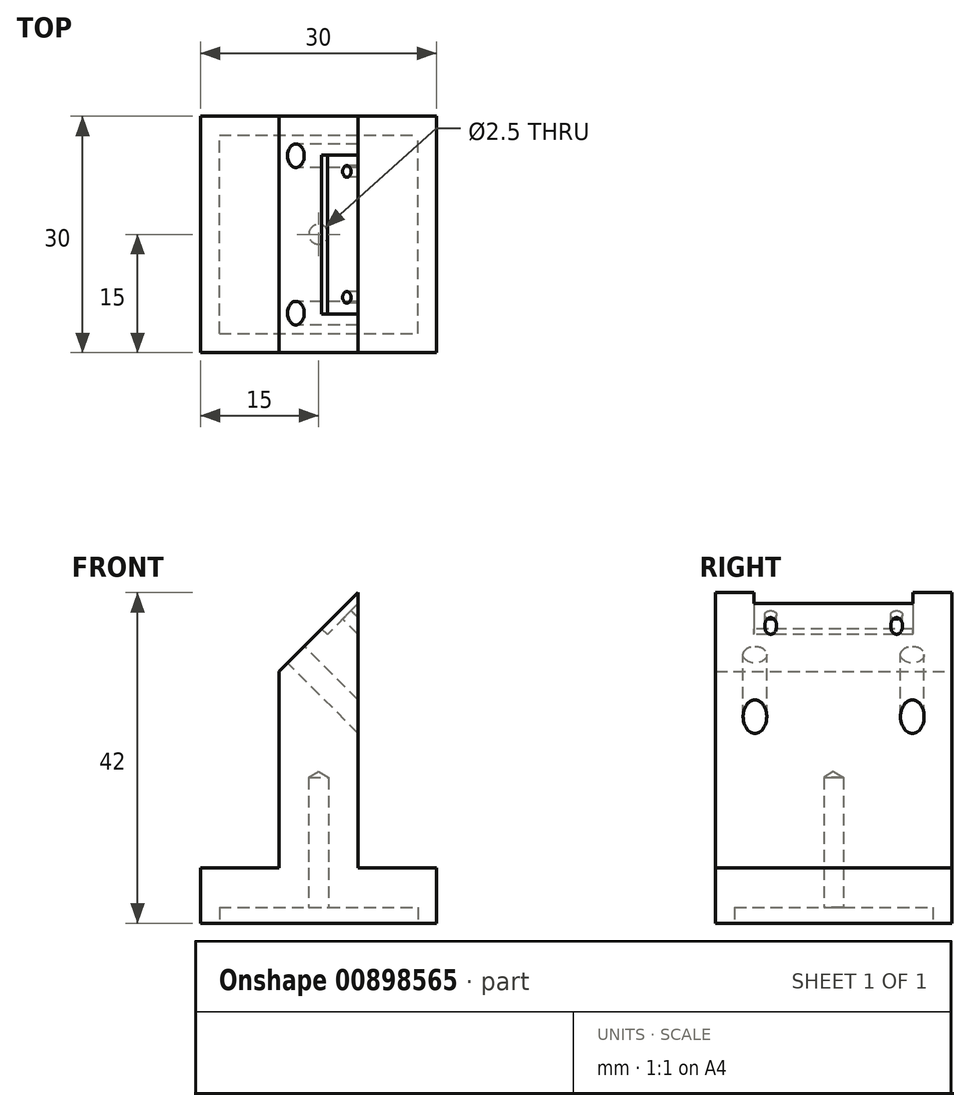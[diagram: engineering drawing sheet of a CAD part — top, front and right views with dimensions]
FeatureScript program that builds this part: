
annotation { "Feature Type Name" : "Feature", "Feature Type Description" : "" }
export const myFeature = defineFeature(function(context is Context, id is Id, definition is map)
    precondition{}
    {
        {
            var Q0;
            Q0=qCreatedBy(makeId("Top.planeOp"),FACE);
            var sketch = newSketch(context, id + "F0", { "sketchPlane" : qUnion([Q0])});
            skLineSegment(sketch, "E0.bottom", {"start": v(-15, 15) * mm, "end": v(15, 15) * mm});
            skLineSegment(sketch, "E0.top", {"start": v(-15, -15) * mm, "end": v(15, -15) * mm});
            skLineSegment(sketch, "E0.left", {"start": v(-15, 15) * mm, "end": v(-15, -15) * mm});
            skLineSegment(sketch, "E0.right", {"start": v(15, 15) * mm, "end": v(15, -15) * mm});
            skLineSegment(sketch, "E1", {"start": v(-15, 15) * mm, "end": v(15, -15) * mm, "construction": true});
            skLineSegment(sketch, "E2", {"start": v(-15, -15) * mm, "end": v(15, 15) * mm, "construction": true});
            skPoint(sketch, "E3", {"position": v(0, 0) * mm});
            skSolve(sketch);
        }
        {
            var Q0;
            Q0 = qSketchRegion(id + "F0", true);
            extrude(context, id + "F1", {"entities" : qUnion([Q0]), "depth" : 7 * mm, "offsetDistance" : 25 * mm});
        }
        {
            var Q0;
            Q0=makeQuery(id+"F1.opExtrude","CAP_FACE",FACE,{"disambiguationData":[OSD([sQuery(id+"F0.wireOp",EDGE,"E0.bottom"),sQuery(id+"F0.wireOp",EDGE,"E0.top"),sQuery(id+"F0.wireOp",EDGE,"E0.left"),sQuery(id+"F0.wireOp",EDGE,"E0.right")])],"isStart":false});
            var sketch = newSketch(context, id + "F2", { "sketchPlane" : qUnion([Q0])});
            skLineSegment(sketch, "E4.bottom", {"start": v(-5, 15) * mm, "end": v(5, 15) * mm});
            skLineSegment(sketch, "E4.top", {"start": v(-5, -15) * mm, "end": v(5, -15) * mm});
            skLineSegment(sketch, "E4.left", {"start": v(-5, 15) * mm, "end": v(-5, -15) * mm});
            skLineSegment(sketch, "E4.right", {"start": v(5, 15) * mm, "end": v(5, -15) * mm});
            skLineSegment(sketch, "E5", {"start": v(5, 15) * mm, "end": v(-5, -15) * mm, "construction": true});
            skLineSegment(sketch, "E6", {"start": v(-15, -15) * mm, "end": v(-15, 15) * mm});
            skLineSegment(sketch, "E7", {"start": v(-5, 15) * mm, "end": v(5, -15) * mm, "construction": true});
            skPoint(sketch, "E8", {"position": v(0, 0) * mm});
            skSolve(sketch);
        }
        {
            var Q0;
            Q0=makeQuery(id+"F2.imprint","IMPRINT",FACE,{"disambiguationData":[TD([[makeQuery(id+"F2.imprint","IMPRINT",EDGE,{"derivedFrom":sQuery(id+"F2.wireOp",EDGE,"E4.bottom")}),-1.0]])]});
            extrude(context, id + "F3", {"entities" : qUnion([Q0]), "operationType" : NewBodyOperationType.ADD, "depth" : 35 * mm, "offsetDistance" : 25 * mm});
        }
        {
            var Q0;
            Q0=makeQuery(id+"F3.opExtrude","CAP_EDGE",EDGE,{"disambiguationData":[OSD([sQuery(id+"F2.wireOp",EDGE,"E4.left")])],"isStart":false});
            chamfer(context, id + "F4", {"entities" : qUnion([Q0]), "width" : 10 * mm, "tangentPropagation" : true});
        }
        {
            var Q0;
            Q0=makeQuery(id+"F1.opExtrude","CAP_FACE",FACE,{"disambiguationData":[OSD([sQuery(id+"F0.wireOp",EDGE,"E0.bottom"),sQuery(id+"F0.wireOp",EDGE,"E0.top"),sQuery(id+"F0.wireOp",EDGE,"E0.left"),sQuery(id+"F0.wireOp",EDGE,"E0.right")])],"isStart":true});
            var sketch = newSketch(context, id + "F5", { "sketchPlane" : qUnion([Q0])});
            skLineSegment(sketch, "E9.bottom", {"start": v(-12.6, 12.6) * mm, "end": v(12.6, 12.6) * mm});
            skLineSegment(sketch, "E9.top", {"start": v(-12.6, -12.6) * mm, "end": v(12.6, -12.6) * mm});
            skLineSegment(sketch, "E9.left", {"start": v(-12.6, 12.6) * mm, "end": v(-12.6, -12.6) * mm});
            skLineSegment(sketch, "E9.right", {"start": v(12.6, 12.6) * mm, "end": v(12.6, -12.6) * mm});
            skPoint(sketch, "E9.middle", {"position": v(0, 0) * mm});
            skSolve(sketch);
        }
        {
            var Q0;
            Q0=makeQuery(id+"F5.imprint","IMPRINT",FACE,{"disambiguationData":[TD([[makeQuery(id+"F5.imprint","IMPRINT",EDGE,{"derivedFrom":sQuery(id+"F5.wireOp",EDGE,"E9.bottom")}),-1.0]])]});
            extrude(context, id + "F6", {"entities" : qUnion([Q0]), "oppositeDirection" : true, "depth" : 2 * mm, "offsetDistance" : 25 * mm});
        }
        {
            var Q0;
            Q0=makeQuery(id+"F6.opExtrude","SWEPT_BODY",BODY,{"disambiguationData":[OSD([sQuery(id+"F5.wireOp",EDGE,"E9.bottom"),sQuery(id+"F5.wireOp",EDGE,"E9.top"),sQuery(id+"F5.wireOp",EDGE,"E9.left"),sQuery(id+"F5.wireOp",EDGE,"E9.right")])]});
            var Q1;
            Q1=makeQuery(id+"F1.opExtrude","SWEPT_BODY",BODY,{"disambiguationData":[OSD([sQuery(id+"F0.wireOp",EDGE,"E0.bottom"),sQuery(id+"F0.wireOp",EDGE,"E0.top"),sQuery(id+"F0.wireOp",EDGE,"E0.left"),sQuery(id+"F0.wireOp",EDGE,"E0.right")])]});
            booleanBodies(context, id + "F7", {"operationType" : BooleanOperationType.SUBTRACTION, "tools" : qUnion([Q0]), "targets" : qUnion([Q1])});
        }
        {
            var Q0;
            Q0=makeQuery(id+"F7.opBoolean","COPY",FACE,{"derivedFrom":makeQuery(id+"F6.opExtrude","CAP_FACE",FACE,{"disambiguationData":[OSD([sQuery(id+"F5.wireOp",EDGE,"E9.bottom"),sQuery(id+"F5.wireOp",EDGE,"E9.top"),sQuery(id+"F5.wireOp",EDGE,"E9.left"),sQuery(id+"F5.wireOp",EDGE,"E9.right")])],"isStart":false})});
            var sketch = newSketch(context, id + "F8", { "sketchPlane" : qUnion([Q0])});
            skPoint(sketch, "E10", {"position": v(0, 0) * mm});
            skSolve(sketch);
        }
        {
            var Q0;
            Q0=sQuery(id+"F8.wireOp",VERTEX,"E10");
            var Q1;
            Q1=makeQuery(id+"F1.opExtrude","SWEPT_BODY",BODY,{"disambiguationData":[OSD([sQuery(id+"F0.wireOp",EDGE,"E0.bottom"),sQuery(id+"F0.wireOp",EDGE,"E0.top"),sQuery(id+"F0.wireOp",EDGE,"E0.left"),sQuery(id+"F0.wireOp",EDGE,"E0.right")])]});
            hole(context, id + "F9", {"style" : HoleStyle.SIMPLE, "endStyle" : HoleEndStyle.BLIND, "standardTappedOrClearance" : lookupTablePath({ "standard" : "ISO", "engagement" : "75%", "pitch" : "0.5 mm", "size" : "M3", "type" : "Tapped" }), "standardBlindInLast" : lookupTablePath({ "standard" : "ISO", "engagement" : "75%", "pitch" : "0.5 mm", "size" : "M3", "type" : "Tapped" }), "holeDiameter" : 2.5 * mm, "majorDiameter" : 3 * mm, "showTappedDepth" : true, "holeDepth" : 16.5 * mm, "tappedDepth" : 15 * mm, "tapClearance" : 3, "locations" : qUnion([Q0]), "scope" : qUnion([Q1])});
        }
        {
            var Q0;
            Q0=makeQuery(id+"F4.opChamfer","BLEND_FACE",FACE,{"disambiguationData":[OSD([sQuery(id+"F2.wireOp",EDGE,"E4.left")])]});
            var sketch = newSketch(context, id + "F10", { "sketchPlane" : qUnion([Q0])});
            skLineSegment(sketch, "E11.bottom", {"start": v(-10.1, 33.23) * mm, "end": v(10.1, 33.23) * mm});
            skLineSegment(sketch, "E11.top", {"start": v(-10.1, 26.73) * mm, "end": v(10.1, 26.73) * mm});
            skLineSegment(sketch, "E11.left", {"start": v(-10.1, 33.23) * mm, "end": v(-10.1, 26.73) * mm});
            skLineSegment(sketch, "E11.right", {"start": v(10.1, 33.23) * mm, "end": v(10.1, 26.73) * mm});
            skSolve(sketch);
        }
        {
            var Q0;
            Q0=makeQuery(id+"F10.imprint","IMPRINT",FACE,{"disambiguationData":[TD([[makeQuery(id+"F10.imprint","IMPRINT",EDGE,{"derivedFrom":sQuery(id+"F10.wireOp",EDGE,"E11.bottom")}),-1.0]])]});
            extrude(context, id + "F11", {"entities" : qUnion([Q0]), "oppositeDirection" : true, "depth" : 1 * mm, "offsetDistance" : 25 * mm});
        }
        {
            var Q0;
            Q0=makeQuery(id+"F11.opExtrude","SWEPT_BODY",BODY,{"disambiguationData":[OSD([sQuery(id+"F10.wireOp",EDGE,"E11.bottom"),sQuery(id+"F10.wireOp",EDGE,"E11.top"),sQuery(id+"F10.wireOp",EDGE,"E11.left"),sQuery(id+"F10.wireOp",EDGE,"E11.right")])]});
            var Q1;
            Q1=makeQuery(id+"F1.opExtrude","SWEPT_BODY",BODY,{"disambiguationData":[OSD([sQuery(id+"F0.wireOp",EDGE,"E0.bottom"),sQuery(id+"F0.wireOp",EDGE,"E0.top"),sQuery(id+"F0.wireOp",EDGE,"E0.left"),sQuery(id+"F0.wireOp",EDGE,"E0.right")])]});
            booleanBodies(context, id + "F12", {"operationType" : BooleanOperationType.SUBTRACTION, "tools" : qUnion([Q0]), "targets" : qUnion([Q1])});
        }
        {
            var Q0;
            Q0=makeQuery(id+"F12.opBoolean","COPY",FACE,{"derivedFrom":makeQuery(id+"F11.opExtrude","CAP_FACE",FACE,{"disambiguationData":[OSD([sQuery(id+"F10.wireOp",EDGE,"E11.bottom"),sQuery(id+"F10.wireOp",EDGE,"E11.top"),sQuery(id+"F10.wireOp",EDGE,"E11.left"),sQuery(id+"F10.wireOp",EDGE,"E11.right")])],"isStart":false})});
            var sketch = newSketch(context, id + "F13", { "sketchPlane" : qUnion([Q0])});
            skPoint(sketch, "E12", {"position": v(-8, 30.23) * mm});
            skPoint(sketch, "E13.MirrorP", {"position": v(8, 30.23) * mm});
            skSolve(sketch);
        }
        {
            var Q0;
            Q0=sQuery(id+"F13.wireOp",VERTEX,"E12");
            var Q1;
            Q1=sQuery(id+"F13.wireOp",VERTEX,"E13.MirrorP");
            var Q2;
            Q2=makeQuery(id+"F1.opExtrude","SWEPT_BODY",BODY,{"disambiguationData":[OSD([sQuery(id+"F0.wireOp",EDGE,"E0.bottom"),sQuery(id+"F0.wireOp",EDGE,"E0.top"),sQuery(id+"F0.wireOp",EDGE,"E0.left"),sQuery(id+"F0.wireOp",EDGE,"E0.right")])]});
            hole(context, id + "F14", {"style" : HoleStyle.SIMPLE, "endStyle" : HoleEndStyle.THROUGH, "holeDiameter" : 1.5 * mm, "majorDiameter" : 3 * mm, "tappedDepth" : 15 * mm, "tapClearance" : 3, "locations" : qUnion([Q0, Q1]), "scope" : qUnion([Q2])});
        }
        {
            var Q0;
            Q0=makeQuery(id+"F4.opChamfer","BLEND_FACE",FACE,{"disambiguationData":[OSD([sQuery(id+"F2.wireOp",EDGE,"E4.left")])]});
            var sketch = newSketch(context, id + "F15", { "sketchPlane" : qUnion([Q0])});
            skPoint(sketch, "E14", {"position": v(-10, 22.1) * mm});
            skPoint(sketch, "E15.MirrorP", {"position": v(10, 22.1) * mm});
            skSolve(sketch);
        }
        {
            var Q0;
            Q0=sQuery(id+"F15.wireOp",VERTEX,"E14");
            var Q1;
            Q1=sQuery(id+"F15.wireOp",VERTEX,"E15.MirrorP");
            var Q2;
            Q2=makeQuery(id+"F1.opExtrude","SWEPT_BODY",BODY,{"disambiguationData":[OSD([sQuery(id+"F0.wireOp",EDGE,"E0.bottom"),sQuery(id+"F0.wireOp",EDGE,"E0.top"),sQuery(id+"F0.wireOp",EDGE,"E0.left"),sQuery(id+"F0.wireOp",EDGE,"E0.right")])]});
            hole(context, id + "F16", {"style" : HoleStyle.SIMPLE, "endStyle" : HoleEndStyle.THROUGH, "holeDiameter" : 3 * mm, "majorDiameter" : 3 * mm, "tappedDepth" : 15 * mm, "tapClearance" : 3, "locations" : qUnion([Q0, Q1]), "scope" : qUnion([Q2])});
        }
    });
